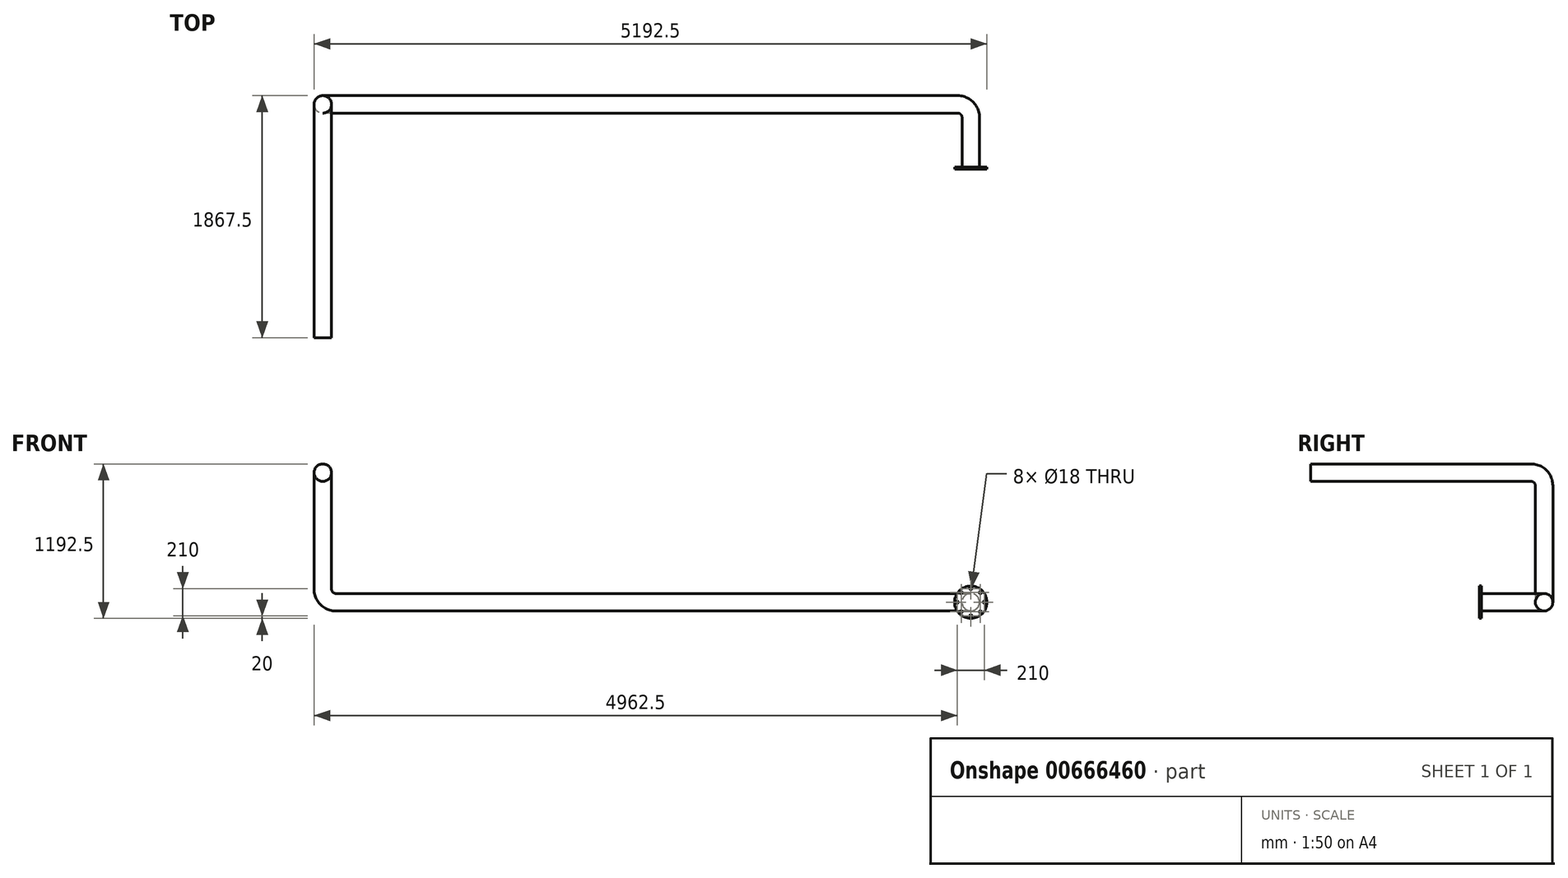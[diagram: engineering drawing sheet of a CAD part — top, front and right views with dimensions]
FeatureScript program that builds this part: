
annotation { "Feature Type Name" : "Feature", "Feature Type Description" : "" }
export const myFeature = defineFeature(function(context is Context, id is Id, definition is map)
    precondition{}
    {
        {
            var Q0;
            Q0=qCreatedBy(makeId("Top.planeOp"),FACE);
            var sketch = newSketch(context, id + "F0", { "sketchPlane" : qUnion([Q0])});
            skLineSegment(sketch, "E0", {"start": v(0, 0) * mm, "end": v(4900, 0) * mm});
            skLineSegment(sketch, "E1", {"start": v(5000, -100) * mm, "end": v(5000, -500) * mm});
            skPoint(sketch, "E2.visualSharp", {"position": v(5000, 0) * mm});
            skArc(sketch, "E2.filletArc", {"start": v(5000, -100) * mm, "mid": v(4970.71, -29.29) * mm, "end": v(4900, 0) * mm});
            skSolve(sketch);
        }
        {
            var Q0;
            Q0=qCreatedBy(makeId("Front.planeOp"),FACE);
            var sketch = newSketch(context, id + "F1", { "sketchPlane" : qUnion([Q0])});
            skLineSegment(sketch, "E3", {"start": v(0, 100) * mm, "end": v(0, 1000) * mm});
            skLineSegment(sketch, "E4.0", {"start": v(100, 0) * mm, "end": v(4900, 0) * mm});
            skPoint(sketch, "E5.visualSharp", {"position": v(0, 0) * mm});
            skArc(sketch, "E5.filletArc", {"start": v(0, 100) * mm, "mid": v(29.29, 29.29) * mm, "end": v(100, 0) * mm});
            skSolve(sketch);
        }
        {
            var Q0;
            Q0=qCreatedBy(makeId("Front.planeOp"),FACE);
            cPlane(context, id + "F2", {"entities" : qUnion([Q0]), "cplaneType" : CPlaneType.OFFSET, "offset" : 500 * mm, "width" : 150 * mm, "height" : 150 * mm});
        }
        {
            var Q0;
            Q0=qCreatedBy(id+"F2.planeOp",FACE);
            var sketch = newSketch(context, id + "F3", { "sketchPlane" : qUnion([Q0])});
            skPoint(sketch, "E6.0", {"position": v(5000, 0) * mm});
            skCircle(sketch, "E7", {"center": v(5000, 0) * mm, "radius": 67.5 * mm});
            skCircle(sketch, "E8", {"center": v(5000, 0) * mm, "radius": 125 * mm});
            skCircle(sketch, "E9", {"center": v(5000, 105) * mm, "radius": 9 * mm});
            skCircle(sketch, "E10.1.0", {"center": v(4925.75, 74.25) * mm, "radius": 9 * mm});
            skCircle(sketch, "E10.2.0", {"center": v(4895, 0) * mm, "radius": 9 * mm});
            skCircle(sketch, "E10.3.0", {"center": v(4925.75, -74.25) * mm, "radius": 9 * mm});
            skCircle(sketch, "E10.4.0", {"center": v(5000, -105) * mm, "radius": 9 * mm});
            skCircle(sketch, "E10.5.0", {"center": v(5074.25, -74.25) * mm, "radius": 9 * mm});
            skCircle(sketch, "E10.6.0", {"center": v(5105, 0) * mm, "radius": 9 * mm});
            skCircle(sketch, "E10.7.0", {"center": v(5074.25, 74.25) * mm, "radius": 9 * mm});
            skSolve(sketch);
        }
        {
            var Q0;
            Q0=qCreatedBy(makeId("Right.planeOp"),FACE);
            var sketch = newSketch(context, id + "F4", { "sketchPlane" : qUnion([Q0])});
            skPoint(sketch, "E11.0", {"position": v(0, 1000) * mm});
            skLineSegment(sketch, "E12", {"start": v(-100, 1000) * mm, "end": v(-1000, 1000) * mm});
            skLineSegment(sketch, "E13.0", {"start": v(0, 100) * mm, "end": v(0, 900) * mm});
            skArc(sketch, "E14.filletArc", {"start": v(0, 900) * mm, "mid": v(-29.29, 970.71) * mm, "end": v(-100, 1000) * mm});
            skSolve(sketch);
        }
        {
            var Q0;
            Q0=makeQuery(id+"F3.imprint","IMPRINT",FACE,{"disambiguationData":[TD([[makeQuery(id+"F3.imprint","IMPRINT",EDGE,{"derivedFrom":sQuery(id+"F3.wireOp",EDGE,"E7")}),1.0]])]});
            var Q1;
            Q1=sQuery(id+"F0.wireOp",EDGE,"E1");
            var Q2;
            Q2=sQuery(id+"F0.wireOp",EDGE,"E2.filletArc");
            var Q3;
            Q3=sQuery(id+"F1.wireOp",EDGE,"E4.0");
            var Q4;
            Q4=sQuery(id+"F1.wireOp",EDGE,"E5.filletArc");
            var Q5;
            Q5=sQuery(id+"F4.wireOp",EDGE,"E13.0");
            var Q6;
            Q6=sQuery(id+"F4.wireOp",EDGE,"E14.filletArc");
            var Q7;
            Q7=sQuery(id+"F4.wireOp",EDGE,"E12");
            sweep(context, id + "F5", {"profiles" : qUnion([Q0]), "path" : qUnion([Q1, Q2, Q3, Q4, Q5, Q6, Q7])});
        }
        {
            var Q0;
            Q0=makeQuery(id+"F3.imprint","IMPRINT",FACE,{"disambiguationData":[TD([[makeQuery(id+"F3.imprint","IMPRINT",EDGE,{"derivedFrom":sQuery(id+"F3.wireOp",EDGE,"E7")}),-1.0]])]});
            extrude(context, id + "F6", {"entities" : qUnion([Q0]), "operationType" : NewBodyOperationType.ADD, "oppositeDirection" : true, "depth" : 15 * mm, "offsetDistance" : 25 * mm});
        }
        {
            var Q0;
            Q0=makeQuery(id+"F5.opSweep","CAP_FACE",FACE,{"disambiguationData":[OSD([sQuery(id+"F3.wireOp",EDGE,"E7"),sQuery(id+"F4.wireOp",VERTEX,"E12.end")])],"isStart":false});
            var sketch = newSketch(context, id + "F7", { "sketchPlane" : qUnion([Q0])});
            skCircle(sketch, "E15.0.0", {"center": v(0, 1000) * mm, "radius": 67.5 * mm});
            skSolve(sketch);
        }
        {
            var Q0;
            Q0=makeQuery(id+"F7.imprint","IMPRINT",FACE,{"disambiguationData":[TD([[makeQuery(id+"F7.imprint","IMPRINT",EDGE,{"derivedFrom":sQuery(id+"F7.wireOp",EDGE,"E15.0.0")}),1.0]])]});
            extrude(context, id + "F8", {"entities" : qUnion([Q0]), "operationType" : NewBodyOperationType.ADD, "depth" : 800 * mm, "offsetDistance" : 25 * mm});
        }
    });
